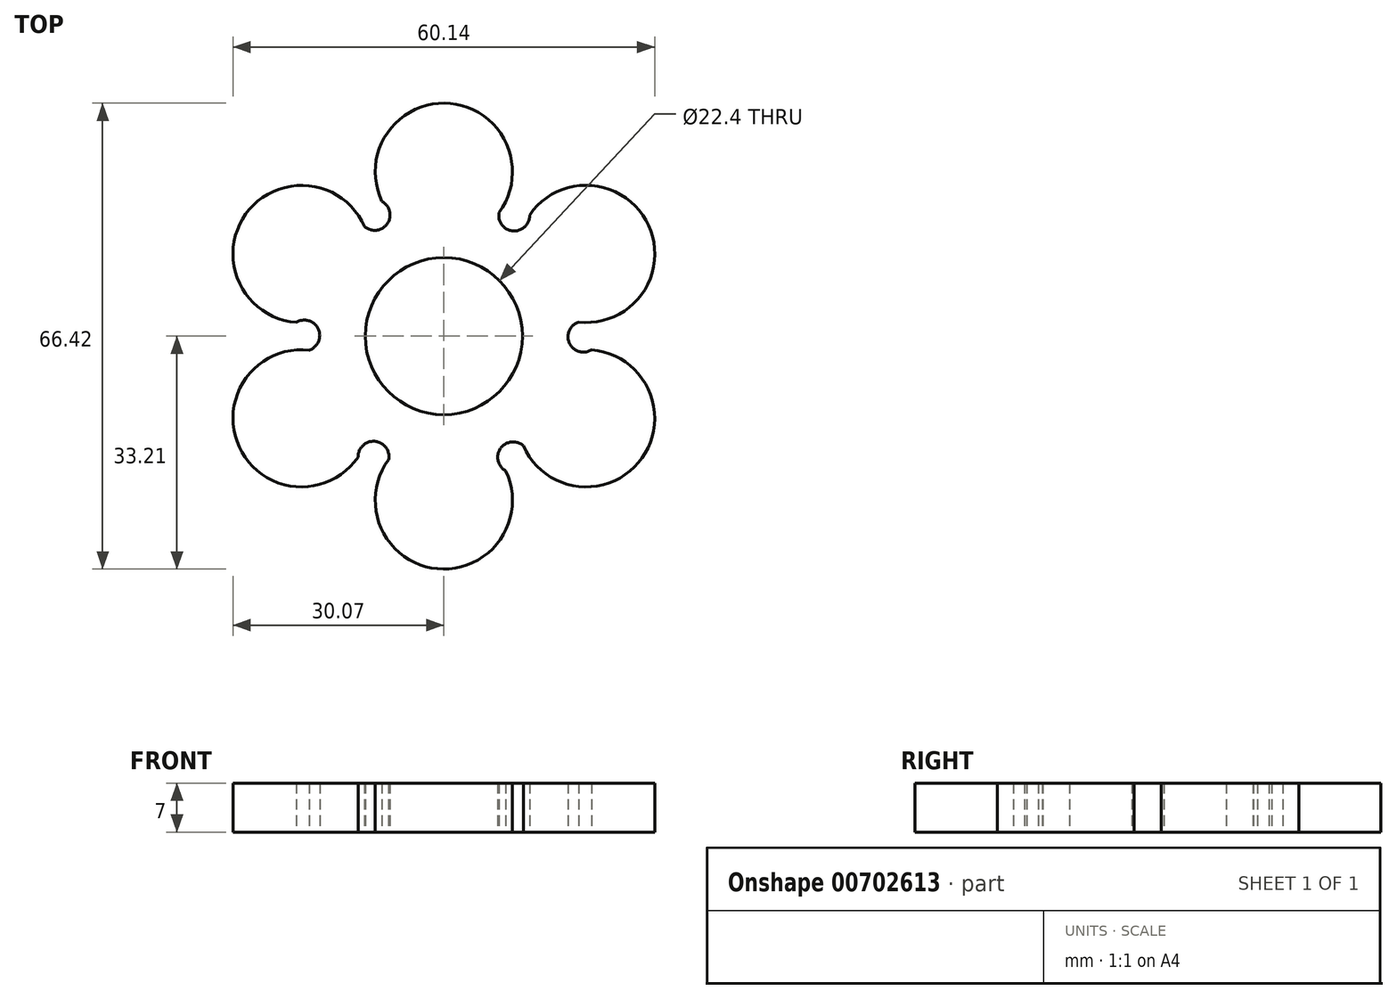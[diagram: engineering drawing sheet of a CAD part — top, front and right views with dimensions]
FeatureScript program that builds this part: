
annotation { "Feature Type Name" : "Feature", "Feature Type Description" : "" }
export const myFeature = defineFeature(function(context is Context, id is Id, definition is map)
    precondition{}
    {
        {
            var Q0;
            Q0=qCreatedBy(makeId("Top.planeOp"),FACE);
            var sketch = newSketch(context, id + "F0", { "sketchPlane" : qUnion([Q0])});
            skCircle(sketch, "E0", {"center": v(0, 0) * mm, "radius": 11.2 * mm});
            skArc(sketch, "E1", {"start": v(7.87, 17.62) * mm, "mid": v(-0.16, 33.2) * mm, "end": v(-7.68, 17.36) * mm});
            skArc(sketch, "E2.1.0", {"start": v(-11.32, 15.63) * mm, "mid": v(-28.84, 16.46) * mm, "end": v(-18.87, 2.03) * mm});
            skArc(sketch, "E2.2.0", {"start": v(-19.2, -2) * mm, "mid": v(-28.67, -16.74) * mm, "end": v(-11.2, -15.33) * mm});
            skArc(sketch, "E2.3.0", {"start": v(-7.87, -17.62) * mm, "mid": v(0.16, -33.2) * mm, "end": v(7.68, -17.36) * mm});
            skArc(sketch, "E2.4.0", {"start": v(11.32, -15.63) * mm, "mid": v(28.84, -16.46) * mm, "end": v(18.87, -2.03) * mm});
            skArc(sketch, "E2.5.0", {"start": v(19.2, 2) * mm, "mid": v(28.67, 16.74) * mm, "end": v(11.2, 15.33) * mm});
            skArc(sketch, "E3", {"start": v(-11.32, 15.63) * mm, "mid": v(-8.07, 16.02) * mm, "end": v(-8.83, 19.2) * mm});
            skArc(sketch, "E4.1.0", {"start": v(-19.2, -2) * mm, "mid": v(-17.9, 1.02) * mm, "end": v(-21.05, 1.96) * mm});
            skArc(sketch, "E4.2.0", {"start": v(-7.87, -17.62) * mm, "mid": v(-9.84, -15) * mm, "end": v(-12.22, -17.25) * mm});
            skArc(sketch, "E4.3.0", {"start": v(11.32, -15.63) * mm, "mid": v(8.07, -16.02) * mm, "end": v(8.83, -19.2) * mm});
            skArc(sketch, "E4.4.0", {"start": v(19.2, 2) * mm, "mid": v(17.9, -1.02) * mm, "end": v(21.05, -1.96) * mm});
            skArc(sketch, "E4.5.0", {"start": v(7.87, 17.62) * mm, "mid": v(9.84, 15) * mm, "end": v(12.22, 17.25) * mm});
            skSolve(sketch);
        }
        {
            var Q0;
            Q0=makeQuery(id+"F0.imprint","IMPRINT",FACE,{"disambiguationData":[TD([[makeQuery(id+"F0.imprint","IMPRINT",EDGE,{"derivedFrom":sQuery(id+"F0.wireOp",EDGE,"E0")}),-1.0]])]});
            extrude(context, id + "F1", {"entities" : qUnion([Q0]), "depth" : 7 * mm, "offsetDistance" : 25 * mm});
        }
    });
